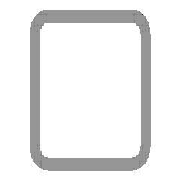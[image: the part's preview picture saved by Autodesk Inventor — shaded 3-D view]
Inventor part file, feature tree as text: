
AUTODESK INVENTOR PART (.ipt)
format: ipt  version: 2025.1 (Build 291241020, 241B)  size: 142,336 bytes
history: native  units: mm (DEFAULTED — no unit token found)
features: other x4, sketch x1, plane x1
ambient origin geometry x8: Origin, YZ Plane, XZ Plane, XY Plane, X Axis, Y Axis, Z Axis, Center Point
bodies: Solid1 (feature_tree), Body (feature_tree)
feature tree (6):
  parser-record x1  (decoder bookkeeping rows leaked as tree rows — omitted from the tree; the rows remain in map.json)
  other  "Driven Length"
  other  "Start Plane"
  other  "End Plane"
  sketch  "Sketch3"  dims[d3=550.0mm d4=0.0mm d7=4.0mm d9=40.0mm d11=40.0mm d12=2.0mm d13=100.0mm d14=650.0mm d15=20.0mm d16=20.0mm d17=90.0deg d18=550.0mm]
  plane  "Work Plane3"
